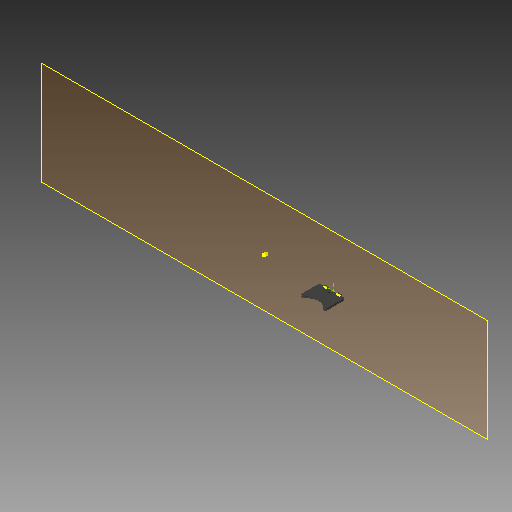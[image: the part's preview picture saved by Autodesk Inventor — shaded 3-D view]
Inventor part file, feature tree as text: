
AUTODESK INVENTOR PART (.ipt)
format: ipt  version: 2017 (Build 210142000, 142)  size: 184,832 bytes
history: native  units: mm
features: sketch x7, extrude x6, fillet x2, reference x2, projected_geometry x2, other x2, plane x1
ambient origin geometry x8: Origin, YZ Plane, XZ Plane, XY Plane, X Axis, Y Axis, Z Axis, Center Point
bodies: Solid1 (feature_tree)
feature tree (22):
  plane  "Work Plane1"
  extrude  "Extrusion1"  Depth=3.0mm
  sketch  "Sketch2"  dims[d2=6.0mm d3=3.0mm]
  extrude  "Extrusion2"  Depth=3.0mm
  extrude  "Extrusion3"  Depth=40.0mm
  fillet  "Fillet1"  Radius=3.0mm
  extrude  "Extrusion4"  Depth=40.0mm
  fillet  "Fillet2"  Radius=38.0mm
  extrude  "Extrusion5"  Depth=16.0mm
  sketch  "Sketch7"  dims[d17=2.0mm d18=40.0mm d19=0.0mm d20=2.0mm d21=1.5mm d22=10.7mm d23=1.5mm d24=6.0mm d25=1.2mm d26=2.0mm d27=40.0mm d28=0.0mm]
  sketch  "Sketch1"  dims[d0=6.0mm d1=3.0mm]
  reference  "Reference1"
  reference  "Reference2"
  projected_geometry  "Projected Loop1"
  projected_geometry  "Projected Loop2"
  sketch  "Sketch3"  dims[d4=3.0mm d5=0.0mm d6=40.0mm d7=3.0mm]
  sketch  "Sketch4"  dims[d8=60.0mm d9=0.0mm d10=40.0mm d11=38.0mm]
  sketch  "Sketch5"  dims[d12=16.0mm d13=16.0mm]
  sketch  "Sketch6"  dims[d14=3.2mm d15=40.0mm d16=0.0mm]
  other  "<userpath>\OneDrive\Inventor\Beast 3D Printer\Extruder Assembly.iam"
  extrude  "Extruder Assembly.iam"  Depth=40.0mm TaperAngle=0.0deg
  other  "Rear Extruder Panel:1"
